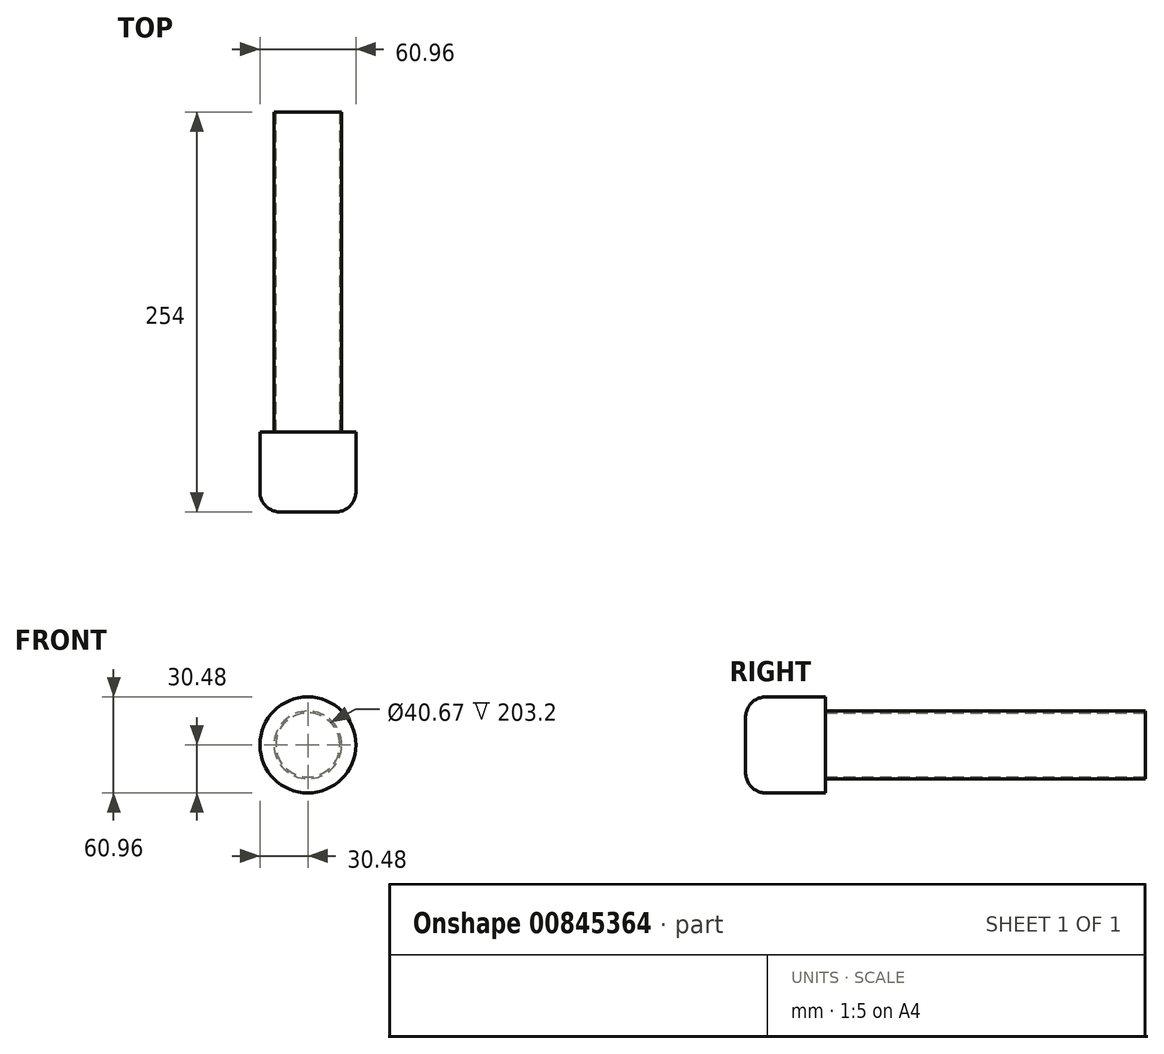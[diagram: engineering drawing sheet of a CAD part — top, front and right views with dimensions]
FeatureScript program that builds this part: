
annotation { "Feature Type Name" : "Feature", "Feature Type Description" : "" }
export const myFeature = defineFeature(function(context is Context, id is Id, definition is map)
    precondition{}
    {
        {
            var Q0;
            Q0=qCreatedBy(makeId("Front.planeOp"),FACE);
            var sketch = newSketch(context, id + "F0", { "sketchPlane" : qUnion([Q0])});
            skCircle(sketch, "E0", {"center": v(0, 0) * mm, "radius": 20.34 * mm});
            skCircle(sketch, "E1", {"center": v(0, 0) * mm, "radius": 21.48 * mm});
            skSolve(sketch);
        }
        {
            var Q0;
            Q0=makeQuery(id+"F0.imprint","IMPRINT",FACE,{"disambiguationData":[TD([[makeQuery(id+"F0.imprint","IMPRINT",EDGE,{"derivedFrom":sQuery(id+"F0.wireOp",EDGE,"E0")}),-1.0]])]});
            extrude(context, id + "F1", {"entities" : qUnion([Q0]), "endBound" : BoundingType.SYMMETRIC, "depth" : 203.2 * mm, "offsetDistance" : 25.4 * mm});
        }
        {
            var Q0;
            Q0=makeQuery(id+"F1.opExtrude","CAP_FACE",FACE,{"disambiguationData":[OSD([sQuery(id+"F0.wireOp",EDGE,"E0"),sQuery(id+"F0.wireOp",EDGE,"E1")])],"isStart":false});
            var sketch = newSketch(context, id + "F2", { "sketchPlane" : qUnion([Q0])});
            skCircle(sketch, "E2", {"center": v(0, 0) * mm, "radius": 30.48 * mm});
            skSolve(sketch);
        }
        {
            var Q0;
            Q0 = qSketchRegion(id + "F2", true);
            extrude(context, id + "F3", {"entities" : qUnion([Q0]), "operationType" : NewBodyOperationType.ADD, "depth" : 50.8 * mm, "offsetDistance" : 25.4 * mm});
        }
        {
            var Q0;
            Q0=makeQuery(id+"F3.opExtrude","CAP_FACE",FACE,{"disambiguationData":[OSD([sQuery(id+"F2.wireOp",EDGE,"E2")])],"isStart":false});
            fillet(context, id + "F4", {"entities" : qUnion([Q0]), "radius" : 12.88 * mm, "tangentPropagation" : true, "allowEdgeOverflow" : false});
        }
    });
